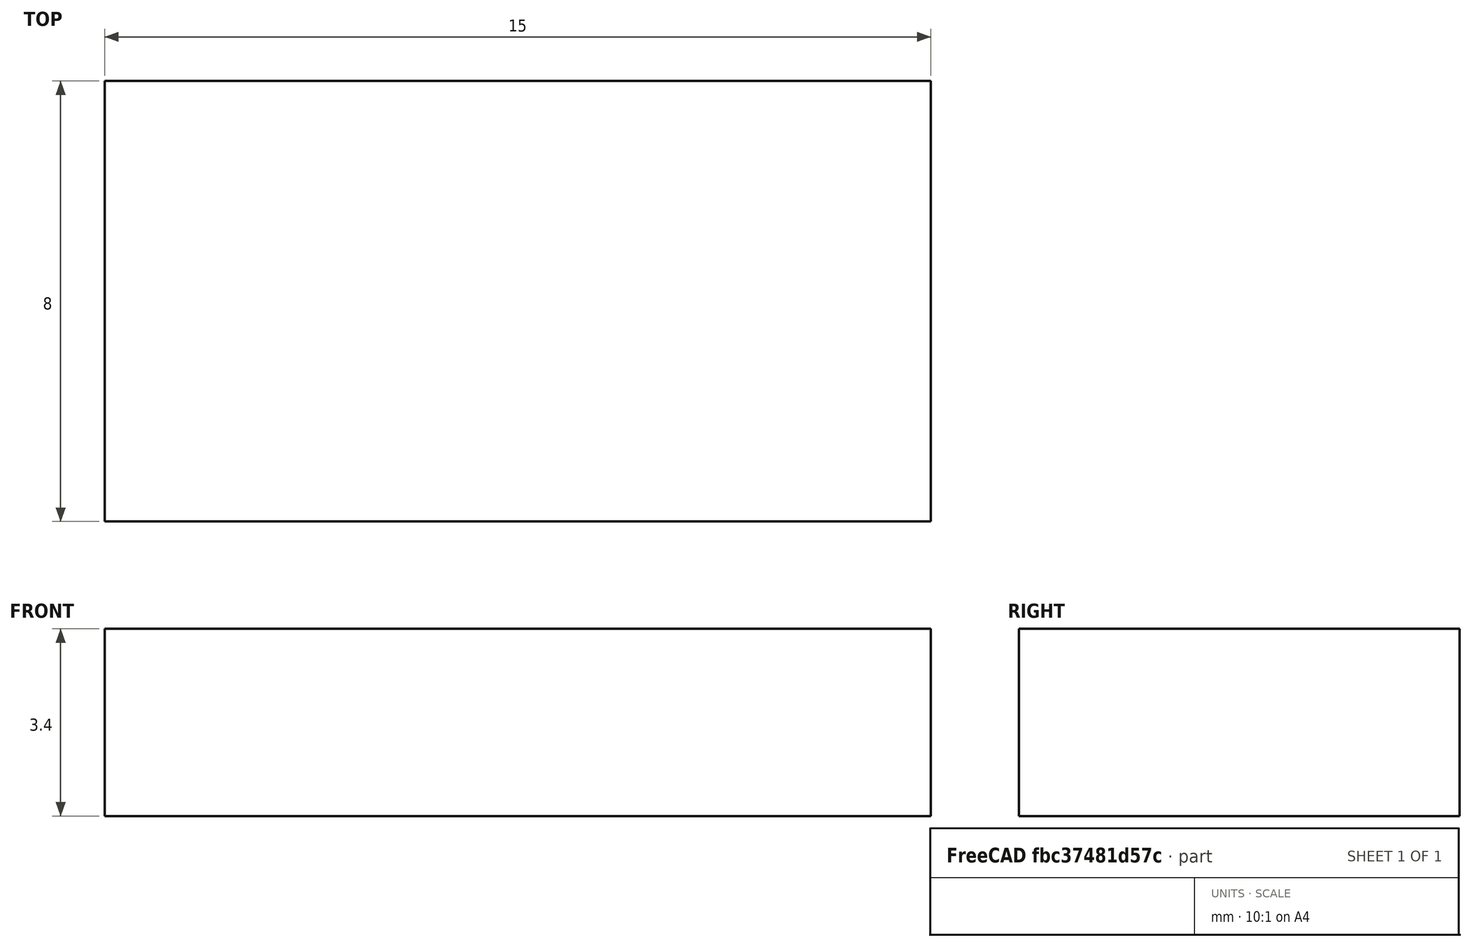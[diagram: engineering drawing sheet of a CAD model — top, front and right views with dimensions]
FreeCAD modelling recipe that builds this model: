
FCSTD DOCUMENT  (FreeCAD 0.18.4R)
Label: bute_arduino
License: All rights reserved
LicenseURL: http://en.wikipedia.org/wiki/All_rights_reserved
objects: Sketcher::SketchObject×1, PartDesign::Pad×1, PartDesign::Body×1
note: 4 computed .brp shape members not serialized (recipe doc carries the construction recipe); baked Part::Feature solids carry a one-line shape summary decoded from their .brp

FEATURE [Sketcher::SketchObject] Sketch
  MapMode = 5
  Support = -> [XY_Plane]
  sketch-geometry (4):
    g0: LineSegment StartX=-7.5 StartY=4 StartZ=0 EndX=7.5 EndY=4 EndZ=0
    g1: LineSegment StartX=7.5 StartY=4 StartZ=0 EndX=7.5 EndY=-4 EndZ=0
    g2: LineSegment StartX=7.5 StartY=-4 StartZ=0 EndX=-7.5 EndY=-4 EndZ=0
    g3: LineSegment StartX=-7.5 StartY=-4 StartZ=0 EndX=-7.5 EndY=4 EndZ=0
  constraints (10):
    c: Coincident(g0,g1)
    c: Coincident(g1,g2)
    c: Coincident(g2,g3)
    c: Coincident(g3,g0)
    c: Horizontal(g2)
    c: Vertical(g1)
    c: DistanceX(g0,g0) = 15
    c: DistanceY(g3,g3) = 8
    c: Symmetric(g0,g0,g-2)
    c: Symmetric(g0,g2,g-1)
FEATURE [PartDesign::Pad] Pad
  Length = 3.4
  Length2 = 100
  Profile = -> Sketch
  Type = 0
FEATURE [PartDesign::Body] Body
  Group = -> [Sketch,Pad]
  Origin = -> Origin
  Tip = -> Pad
